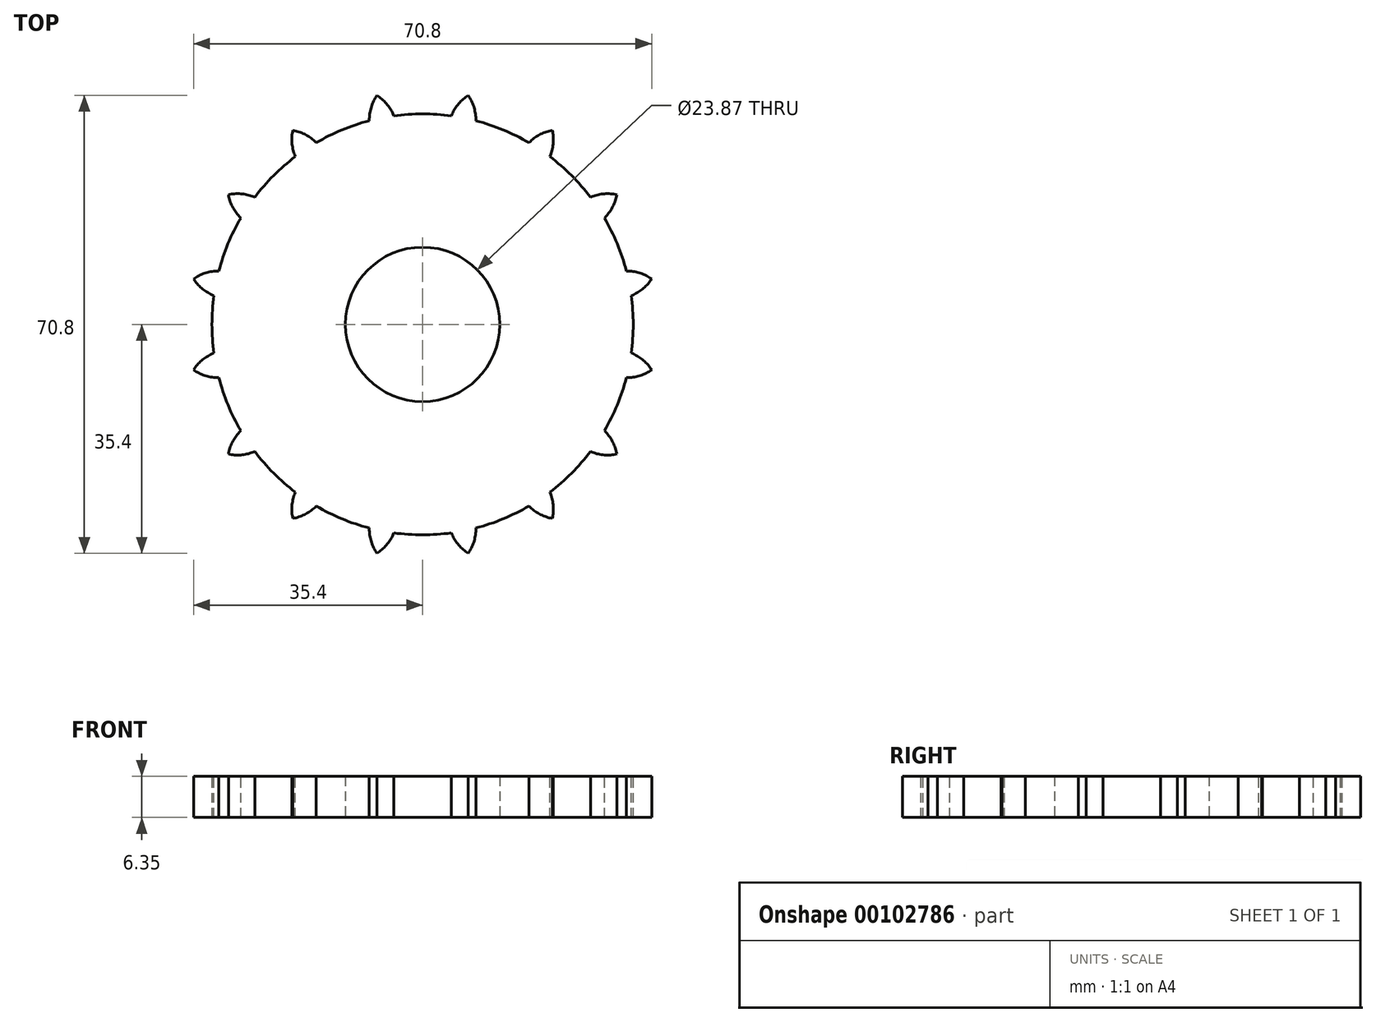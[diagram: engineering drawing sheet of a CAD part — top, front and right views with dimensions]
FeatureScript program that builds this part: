
annotation { "Feature Type Name" : "Feature", "Feature Type Description" : "" }
export const myFeature = defineFeature(function(context is Context, id is Id, definition is map)
    precondition{}
    {
        {
            var Q0;
            Q0=qCreatedBy(makeId("Top.planeOp"),FACE);
            var sketch = newSketch(context, id + "F0", { "sketchPlane" : qUnion([Q0])});
            skCircle(sketch, "E0", {"center": v(0, 0) * mm, "radius": 44.45 * mm});
            skCircle(sketch, "E1", {"center": v(0, 0) * mm, "radius": 25.4 * mm});
            skCircle(sketch, "E2", {"center": v(0, 0) * mm, "radius": 50.44 * mm, "construction": true});
            skCircle(sketch, "E3", {"center": v(0, 0) * mm, "radius": 11.93 * mm});
            skSolve(sketch);
        }
        {
            var Q0;
            Q0 = qSketchRegion(id + "F0", true);
            var Q1;
            Q1=makeQuery(id+"F0.imprint","IMPRINT",FACE,{"disambiguationData":[TD([[makeQuery(id+"F0.imprint","IMPRINT",EDGE,{"derivedFrom":sQuery(id+"F0.wireOp",EDGE,"E1")}),1.0]])]});
            extrude(context, id + "F1", {"entities" : qUnion([Q0, Q1]), "depth" : 6.35 * mm});
        }
        {
            var Q0;
            Q0=makeQuery(id+"F1.opExtrude","CAP_FACE",FACE,{"disambiguationData":[OSD([sQuery(id+"F0.wireOp",EDGE,"E0"),sQuery(id+"F0.wireOp",EDGE,"E1")])],"isStart":false});
            var sketch = newSketch(context, id + "F2", { "sketchPlane" : qUnion([Q0])});
            skCircle(sketch, "E4", {"center": v(0, 0) * mm, "radius": 32.55 * mm});
            skLineSegment(sketch, "E5", {"start": v(0, 0) * mm, "end": v(0, 32.55) * mm, "construction": true});
            skLineSegment(sketch, "E6", {"start": v(0, 32.55) * mm, "end": v(18.37, 32.55) * mm, "construction": true});
            skLineSegment(sketch, "E7", {"start": v(0, 32.55) * mm, "end": v(5, 36.56) * mm, "construction": true});
            skLineSegment(sketch, "E8", {"start": v(5, 36.56) * mm, "end": v(-4.46, 32.3) * mm, "construction": true});
            skLineSegment(sketch, "E9", {"start": v(-4.46, 32.3) * mm, "end": v(-7.22, 38.43) * mm, "construction": true});
            skLineSegment(sketch, "E10", {"start": v(0, 0) * mm, "end": v(-7.04, 35.4) * mm, "construction": true});
            skArc(sketch, "E11", {"start": v(-7.04, 35.4) * mm, "mid": v(-15.56, 25.52) * mm, "end": v(-4.57, 32.54) * mm, "construction": true});
            skLineSegment(sketch, "E12", {"start": v(-4.57, 32.54) * mm, "end": v(-4.57, 32.54) * mm});
            skArc(sketch, "E13", {"start": v(-4.57, 32.54) * mm, "mid": v(-5.6, 34.15) * mm, "end": v(-7.04, 35.4) * mm});
            skArc(sketch, "E14", {"start": v(-3.1, 30.07) * mm, "mid": v(13.81, 42) * mm, "end": v(-4.43, 32.25) * mm, "construction": true});
            skArc(sketch, "E15", {"start": v(-4.43, 32.25) * mm, "mid": v(-3.83, 31.12) * mm, "end": v(-3.1, 30.07) * mm});
            skArc(sketch, "E16.MirrorCS", {"start": v(4.57, 32.54) * mm, "mid": v(5.6, 34.15) * mm, "end": v(7.04, 35.4) * mm});
            skArc(sketch, "E17.MirrorCS", {"start": v(4.43, 32.25) * mm, "mid": v(3.83, 31.12) * mm, "end": v(3.1, 30.07) * mm});
            skLineSegment(sketch, "E18", {"start": v(-4.57, 32.54) * mm, "end": v(-4.46, 32.3) * mm});
            skLineSegment(sketch, "E19", {"start": v(4.57, 32.54) * mm, "end": v(4.43, 32.25) * mm});
            skArc(sketch, "E20", {"start": v(3.1, 30.07) * mm, "mid": v(0, 36.51) * mm, "end": v(-3.1, 30.07) * mm, "construction": true});
            skArc(sketch, "E21", {"start": v(-3.1, 30.07) * mm, "mid": v(0, 28.59) * mm, "end": v(3.1, 30.07) * mm});
            skLineSegment(sketch, "E22", {"start": v(-4.46, 32.3) * mm, "end": v(-4.43, 32.25) * mm});
            skArc(sketch, "E23.1.0", {"start": v(-16.67, 28.32) * mm, "mid": v(-18.24, 29.41) * mm, "end": v(-20.05, 30) * mm});
            skArc(sketch, "E23.1.1", {"start": v(-16.44, 28.1) * mm, "mid": v(-15.45, 27.28) * mm, "end": v(-14.36, 26.6) * mm});
            skArc(sketch, "E23.1.2", {"start": v(-8.24, 31.81) * mm, "mid": v(-7.9, 33.7) * mm, "end": v(-7.04, 35.4) * mm});
            skLineSegment(sketch, "E23.1.3", {"start": v(-8.24, 31.81) * mm, "end": v(-8.25, 31.49) * mm});
            skArc(sketch, "E23.1.4", {"start": v(-8.25, 31.49) * mm, "mid": v(-8.37, 30.21) * mm, "end": v(-8.65, 28.96) * mm});
            skArc(sketch, "E23.1.5", {"start": v(-14.36, 26.6) * mm, "mid": v(-10.94, 26.41) * mm, "end": v(-8.65, 28.96) * mm});
            skArc(sketch, "E23.2.0", {"start": v(-26.24, 19.78) * mm, "mid": v(-28.1, 20.2) * mm, "end": v(-30, 20.05) * mm});
            skArc(sketch, "E23.2.1", {"start": v(-25.94, 19.67) * mm, "mid": v(-24.71, 19.3) * mm, "end": v(-23.45, 19.08) * mm});
            skArc(sketch, "E23.2.2", {"start": v(-19.78, 26.24) * mm, "mid": v(-20.2, 28.1) * mm, "end": v(-20.05, 30) * mm});
            skLineSegment(sketch, "E23.2.3", {"start": v(-19.78, 26.24) * mm, "end": v(-19.67, 25.94) * mm});
            skArc(sketch, "E23.2.4", {"start": v(-19.67, 25.94) * mm, "mid": v(-19.3, 24.71) * mm, "end": v(-19.08, 23.45) * mm});
            skArc(sketch, "E23.2.5", {"start": v(-23.45, 19.08) * mm, "mid": v(-20.21, 20.21) * mm, "end": v(-19.08, 23.45) * mm});
            skLineSegment(sketch, "E24", {"start": v(-4.43, 32.25) * mm, "end": v(-4.43, 32.25) * mm});
            skArc(sketch, "E25.3.0", {"start": v(-31.81, 8.24) * mm, "mid": v(-33.7, 7.9) * mm, "end": v(-35.4, 7.04) * mm});
            skArc(sketch, "E25.3.1", {"start": v(-31.49, 8.25) * mm, "mid": v(-30.21, 8.37) * mm, "end": v(-28.96, 8.65) * mm});
            skArc(sketch, "E25.3.2", {"start": v(-28.32, 16.67) * mm, "mid": v(-29.41, 18.24) * mm, "end": v(-30, 20.05) * mm});
            skArc(sketch, "E25.3.3", {"start": v(-28.1, 16.44) * mm, "mid": v(-27.28, 15.45) * mm, "end": v(-26.6, 14.36) * mm});
            skLineSegment(sketch, "E25.3.4", {"start": v(-28.32, 16.67) * mm, "end": v(-28.1, 16.44) * mm});
            skArc(sketch, "E25.3.5", {"start": v(-28.96, 8.65) * mm, "mid": v(-26.41, 10.94) * mm, "end": v(-26.6, 14.36) * mm});
            skArc(sketch, "E25.4.0", {"start": v(-32.54, -4.57) * mm, "mid": v(-34.15, -5.6) * mm, "end": v(-35.4, -7.04) * mm});
            skArc(sketch, "E25.4.1", {"start": v(-32.25, -4.43) * mm, "mid": v(-31.12, -3.83) * mm, "end": v(-30.07, -3.1) * mm});
            skArc(sketch, "E25.4.2", {"start": v(-32.54, 4.57) * mm, "mid": v(-34.15, 5.6) * mm, "end": v(-35.4, 7.04) * mm});
            skArc(sketch, "E25.4.3", {"start": v(-32.25, 4.43) * mm, "mid": v(-31.12, 3.83) * mm, "end": v(-30.07, 3.1) * mm});
            skLineSegment(sketch, "E25.4.4", {"start": v(-32.54, 4.57) * mm, "end": v(-32.25, 4.43) * mm});
            skArc(sketch, "E25.4.5", {"start": v(-30.07, -3.1) * mm, "mid": v(-28.59, 0) * mm, "end": v(-30.07, 3.1) * mm});
            skArc(sketch, "E25.5.0", {"start": v(-28.32, -16.67) * mm, "mid": v(-29.41, -18.24) * mm, "end": v(-30, -20.05) * mm});
            skArc(sketch, "E25.5.1", {"start": v(-28.1, -16.44) * mm, "mid": v(-27.28, -15.45) * mm, "end": v(-26.6, -14.36) * mm});
            skArc(sketch, "E25.5.2", {"start": v(-31.81, -8.24) * mm, "mid": v(-33.7, -7.9) * mm, "end": v(-35.4, -7.04) * mm});
            skArc(sketch, "E25.5.3", {"start": v(-31.49, -8.25) * mm, "mid": v(-30.21, -8.37) * mm, "end": v(-28.96, -8.65) * mm});
            skLineSegment(sketch, "E25.5.4", {"start": v(-31.81, -8.24) * mm, "end": v(-31.49, -8.25) * mm});
            skArc(sketch, "E25.5.5", {"start": v(-26.6, -14.36) * mm, "mid": v(-26.41, -10.94) * mm, "end": v(-28.96, -8.65) * mm});
            skArc(sketch, "E25.6.0", {"start": v(-19.78, -26.24) * mm, "mid": v(-20.2, -28.1) * mm, "end": v(-20.05, -30) * mm});
            skArc(sketch, "E25.6.1", {"start": v(-19.67, -25.94) * mm, "mid": v(-19.3, -24.71) * mm, "end": v(-19.08, -23.45) * mm});
            skArc(sketch, "E25.6.2", {"start": v(-26.24, -19.78) * mm, "mid": v(-28.1, -20.2) * mm, "end": v(-30, -20.05) * mm});
            skArc(sketch, "E25.6.3", {"start": v(-25.94, -19.67) * mm, "mid": v(-24.71, -19.3) * mm, "end": v(-23.45, -19.08) * mm});
            skLineSegment(sketch, "E25.6.4", {"start": v(-26.24, -19.78) * mm, "end": v(-25.94, -19.67) * mm});
            skArc(sketch, "E25.6.5", {"start": v(-19.08, -23.45) * mm, "mid": v(-20.21, -20.21) * mm, "end": v(-23.45, -19.08) * mm});
            skArc(sketch, "E25.7.0", {"start": v(-8.24, -31.81) * mm, "mid": v(-7.9, -33.7) * mm, "end": v(-7.04, -35.4) * mm});
            skArc(sketch, "E25.7.1", {"start": v(-8.25, -31.49) * mm, "mid": v(-8.37, -30.21) * mm, "end": v(-8.65, -28.96) * mm});
            skArc(sketch, "E25.7.2", {"start": v(-16.67, -28.32) * mm, "mid": v(-18.24, -29.41) * mm, "end": v(-20.05, -30) * mm});
            skArc(sketch, "E25.7.3", {"start": v(-16.44, -28.1) * mm, "mid": v(-15.45, -27.28) * mm, "end": v(-14.36, -26.6) * mm});
            skLineSegment(sketch, "E25.7.4", {"start": v(-16.67, -28.32) * mm, "end": v(-16.44, -28.1) * mm});
            skArc(sketch, "E25.7.5", {"start": v(-8.65, -28.96) * mm, "mid": v(-10.94, -26.41) * mm, "end": v(-14.36, -26.6) * mm});
            skArc(sketch, "E25.8.0", {"start": v(4.57, -32.54) * mm, "mid": v(5.6, -34.15) * mm, "end": v(7.04, -35.4) * mm});
            skArc(sketch, "E25.8.1", {"start": v(4.43, -32.25) * mm, "mid": v(3.83, -31.12) * mm, "end": v(3.1, -30.07) * mm});
            skArc(sketch, "E25.8.2", {"start": v(-4.57, -32.54) * mm, "mid": v(-5.6, -34.15) * mm, "end": v(-7.04, -35.4) * mm});
            skArc(sketch, "E25.8.3", {"start": v(-4.43, -32.25) * mm, "mid": v(-3.83, -31.12) * mm, "end": v(-3.1, -30.07) * mm});
            skLineSegment(sketch, "E25.8.4", {"start": v(-4.57, -32.54) * mm, "end": v(-4.43, -32.25) * mm});
            skArc(sketch, "E25.8.5", {"start": v(3.1, -30.07) * mm, "mid": v(0, -28.59) * mm, "end": v(-3.1, -30.07) * mm});
            skArc(sketch, "E25.9.0", {"start": v(16.67, -28.32) * mm, "mid": v(18.24, -29.41) * mm, "end": v(20.05, -30) * mm});
            skArc(sketch, "E25.9.1", {"start": v(16.44, -28.1) * mm, "mid": v(15.45, -27.28) * mm, "end": v(14.36, -26.6) * mm});
            skArc(sketch, "E25.9.2", {"start": v(8.24, -31.81) * mm, "mid": v(7.9, -33.7) * mm, "end": v(7.04, -35.4) * mm});
            skArc(sketch, "E25.9.3", {"start": v(8.25, -31.49) * mm, "mid": v(8.37, -30.21) * mm, "end": v(8.65, -28.96) * mm});
            skLineSegment(sketch, "E25.9.4", {"start": v(8.24, -31.81) * mm, "end": v(8.25, -31.49) * mm});
            skArc(sketch, "E25.9.5", {"start": v(14.36, -26.6) * mm, "mid": v(10.94, -26.41) * mm, "end": v(8.65, -28.96) * mm});
            skArc(sketch, "E25.10.0", {"start": v(26.24, -19.78) * mm, "mid": v(28.1, -20.2) * mm, "end": v(30, -20.05) * mm});
            skArc(sketch, "E25.10.1", {"start": v(25.94, -19.67) * mm, "mid": v(24.71, -19.3) * mm, "end": v(23.45, -19.08) * mm});
            skArc(sketch, "E25.10.2", {"start": v(19.78, -26.24) * mm, "mid": v(20.2, -28.1) * mm, "end": v(20.05, -30) * mm});
            skArc(sketch, "E25.10.3", {"start": v(19.67, -25.94) * mm, "mid": v(19.3, -24.71) * mm, "end": v(19.08, -23.45) * mm});
            skLineSegment(sketch, "E25.10.4", {"start": v(19.78, -26.24) * mm, "end": v(19.67, -25.94) * mm});
            skArc(sketch, "E25.10.5", {"start": v(23.45, -19.08) * mm, "mid": v(20.21, -20.21) * mm, "end": v(19.08, -23.45) * mm});
            skArc(sketch, "E25.11.0", {"start": v(31.81, -8.24) * mm, "mid": v(33.7, -7.9) * mm, "end": v(35.4, -7.04) * mm});
            skArc(sketch, "E25.11.1", {"start": v(31.49, -8.25) * mm, "mid": v(30.21, -8.37) * mm, "end": v(28.96, -8.65) * mm});
            skArc(sketch, "E25.11.2", {"start": v(28.32, -16.67) * mm, "mid": v(29.41, -18.24) * mm, "end": v(30, -20.05) * mm});
            skArc(sketch, "E25.11.3", {"start": v(28.1, -16.44) * mm, "mid": v(27.28, -15.45) * mm, "end": v(26.6, -14.36) * mm});
            skLineSegment(sketch, "E25.11.4", {"start": v(28.32, -16.67) * mm, "end": v(28.1, -16.44) * mm});
            skArc(sketch, "E25.11.5", {"start": v(28.96, -8.65) * mm, "mid": v(26.41, -10.94) * mm, "end": v(26.6, -14.36) * mm});
            skArc(sketch, "E25.12.0", {"start": v(32.54, 4.57) * mm, "mid": v(34.15, 5.6) * mm, "end": v(35.4, 7.04) * mm});
            skArc(sketch, "E25.12.1", {"start": v(32.25, 4.43) * mm, "mid": v(31.12, 3.83) * mm, "end": v(30.07, 3.1) * mm});
            skArc(sketch, "E25.12.2", {"start": v(32.54, -4.57) * mm, "mid": v(34.15, -5.6) * mm, "end": v(35.4, -7.04) * mm});
            skArc(sketch, "E25.12.3", {"start": v(32.25, -4.43) * mm, "mid": v(31.12, -3.83) * mm, "end": v(30.07, -3.1) * mm});
            skLineSegment(sketch, "E25.12.4", {"start": v(32.54, -4.57) * mm, "end": v(32.25, -4.43) * mm});
            skArc(sketch, "E25.12.5", {"start": v(30.07, 3.1) * mm, "mid": v(28.59, 0) * mm, "end": v(30.07, -3.1) * mm});
            skArc(sketch, "E25.13.0", {"start": v(28.32, 16.67) * mm, "mid": v(29.41, 18.24) * mm, "end": v(30, 20.05) * mm});
            skArc(sketch, "E25.13.1", {"start": v(28.1, 16.44) * mm, "mid": v(27.28, 15.45) * mm, "end": v(26.6, 14.36) * mm});
            skArc(sketch, "E25.13.2", {"start": v(31.81, 8.24) * mm, "mid": v(33.7, 7.9) * mm, "end": v(35.4, 7.04) * mm});
            skArc(sketch, "E25.13.3", {"start": v(31.49, 8.25) * mm, "mid": v(30.21, 8.37) * mm, "end": v(28.96, 8.65) * mm});
            skLineSegment(sketch, "E25.13.4", {"start": v(31.81, 8.24) * mm, "end": v(31.49, 8.25) * mm});
            skArc(sketch, "E25.13.5", {"start": v(26.6, 14.36) * mm, "mid": v(26.41, 10.94) * mm, "end": v(28.96, 8.65) * mm});
            skArc(sketch, "E25.14.0", {"start": v(19.78, 26.24) * mm, "mid": v(20.2, 28.1) * mm, "end": v(20.05, 30) * mm});
            skArc(sketch, "E25.14.1", {"start": v(19.67, 25.94) * mm, "mid": v(19.3, 24.71) * mm, "end": v(19.08, 23.45) * mm});
            skArc(sketch, "E25.14.2", {"start": v(26.24, 19.78) * mm, "mid": v(28.1, 20.2) * mm, "end": v(30, 20.05) * mm});
            skArc(sketch, "E25.14.3", {"start": v(25.94, 19.67) * mm, "mid": v(24.71, 19.3) * mm, "end": v(23.45, 19.08) * mm});
            skLineSegment(sketch, "E25.14.4", {"start": v(26.24, 19.78) * mm, "end": v(25.94, 19.67) * mm});
            skArc(sketch, "E25.14.5", {"start": v(19.08, 23.45) * mm, "mid": v(20.21, 20.21) * mm, "end": v(23.45, 19.08) * mm});
            skArc(sketch, "E25.15.0", {"start": v(8.24, 31.81) * mm, "mid": v(7.9, 33.7) * mm, "end": v(7.04, 35.4) * mm});
            skArc(sketch, "E25.15.1", {"start": v(8.25, 31.49) * mm, "mid": v(8.37, 30.21) * mm, "end": v(8.65, 28.96) * mm});
            skArc(sketch, "E25.15.2", {"start": v(16.67, 28.32) * mm, "mid": v(18.24, 29.41) * mm, "end": v(20.05, 30) * mm});
            skArc(sketch, "E25.15.3", {"start": v(16.44, 28.1) * mm, "mid": v(15.45, 27.28) * mm, "end": v(14.36, 26.6) * mm});
            skLineSegment(sketch, "E25.15.4", {"start": v(16.67, 28.32) * mm, "end": v(16.44, 28.1) * mm});
            skArc(sketch, "E25.15.5", {"start": v(8.65, 28.96) * mm, "mid": v(10.94, 26.41) * mm, "end": v(14.36, 26.6) * mm});
            skLineSegment(sketch, "E26", {"start": v(-4.57, 32.54) * mm, "end": v(-4.43, 32.25) * mm});
            skLineSegment(sketch, "E27", {"start": v(8.24, 31.81) * mm, "end": v(8.25, 31.49) * mm});
            skLineSegment(sketch, "E28", {"start": v(28.32, 16.67) * mm, "end": v(28.1, 16.44) * mm});
            skLineSegment(sketch, "E29", {"start": v(32.54, 4.57) * mm, "end": v(32.25, 4.43) * mm});
            skLineSegment(sketch, "E30", {"start": v(19.78, 26.24) * mm, "end": v(19.67, 25.94) * mm});
            skLineSegment(sketch, "E31", {"start": v(31.81, -8.24) * mm, "end": v(31.49, -8.25) * mm});
            skLineSegment(sketch, "E32", {"start": v(26.24, -19.78) * mm, "end": v(25.94, -19.67) * mm});
            skLineSegment(sketch, "E33", {"start": v(16.67, -28.32) * mm, "end": v(16.44, -28.1) * mm});
            skLineSegment(sketch, "E34", {"start": v(4.57, -32.54) * mm, "end": v(4.43, -32.25) * mm});
            skLineSegment(sketch, "E35", {"start": v(-8.24, -31.81) * mm, "end": v(-8.25, -31.49) * mm});
            skLineSegment(sketch, "E36", {"start": v(-19.78, -26.24) * mm, "end": v(-19.67, -25.94) * mm});
            skLineSegment(sketch, "E37", {"start": v(-28.32, -16.67) * mm, "end": v(-28.1, -16.44) * mm});
            skLineSegment(sketch, "E38", {"start": v(-32.54, -4.57) * mm, "end": v(-32.25, -4.43) * mm});
            skLineSegment(sketch, "E39", {"start": v(-31.81, 8.24) * mm, "end": v(-31.49, 8.25) * mm});
            skLineSegment(sketch, "E40", {"start": v(-26.24, 19.78) * mm, "end": v(-25.94, 19.67) * mm});
            skLineSegment(sketch, "E41", {"start": v(-16.67, 28.32) * mm, "end": v(-16.44, 28.1) * mm});
            skCircle(sketch, "E42", {"center": v(0, 0) * mm, "radius": 28.15 * mm, "construction": true});
            skSolve(sketch);
        }
        {
            var Q0;
            Q0 = qSketchRegion(id + "F2", true);
            extrude(context, id + "F3", {"entities" : qUnion([Q0]), "operationType" : NewBodyOperationType.INTERSECT, "oppositeDirection" : true, "depth" : 6.35 * mm});
        }
    });
